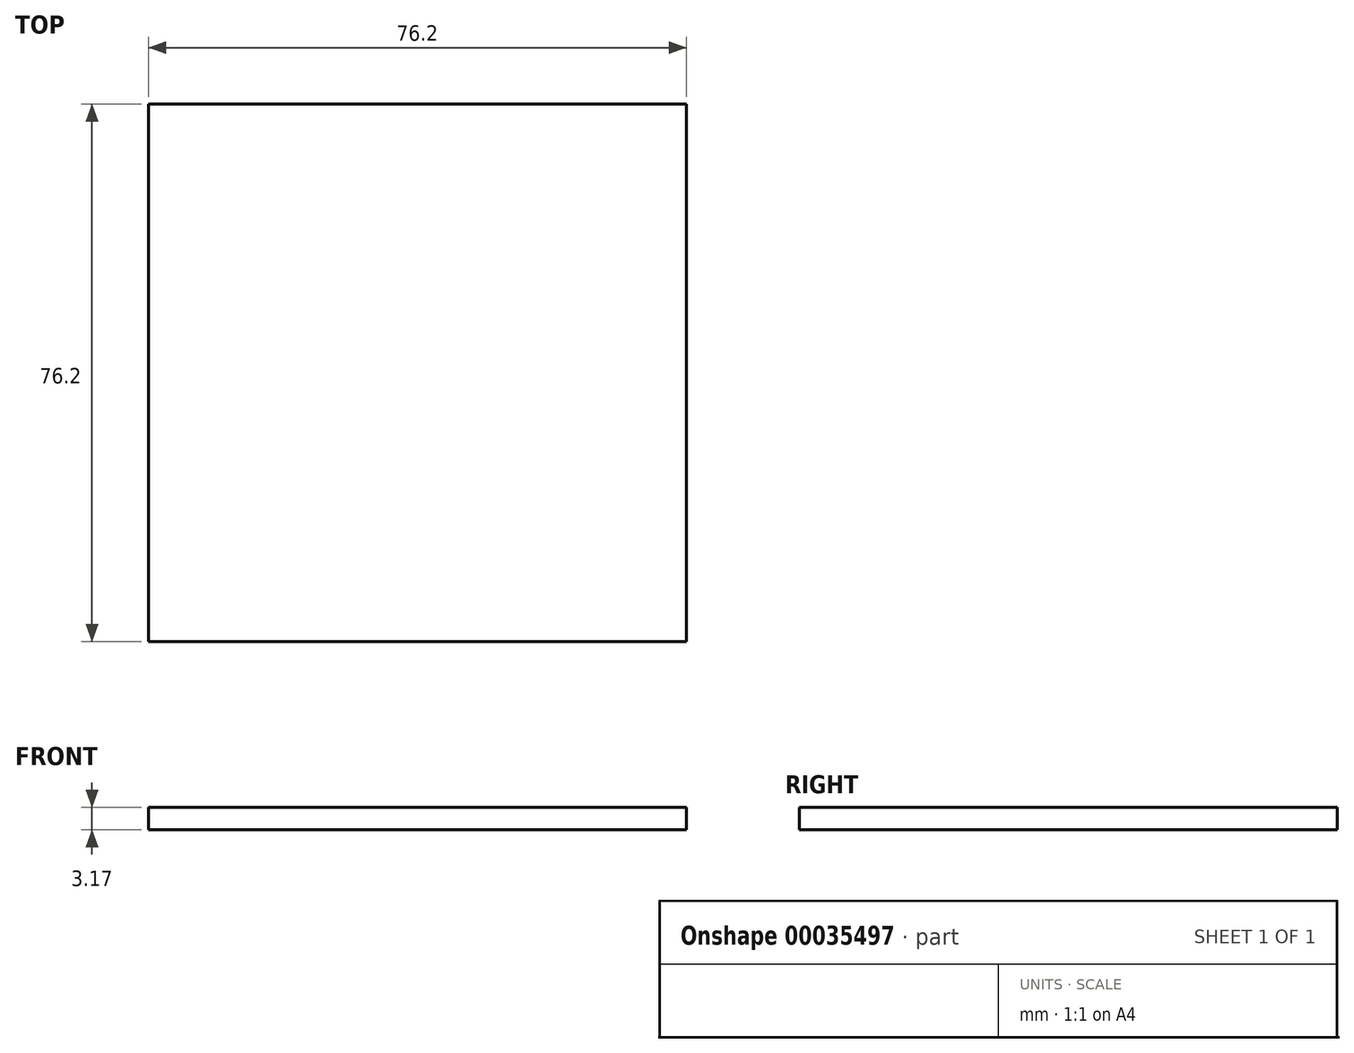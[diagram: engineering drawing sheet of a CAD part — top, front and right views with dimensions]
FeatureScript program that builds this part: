
annotation { "Feature Type Name" : "Feature", "Feature Type Description" : "" }
export const myFeature = defineFeature(function(context is Context, id is Id, definition is map)
    precondition{}
    {
        {
            var Q0;
            Q0=qCreatedBy(makeId("Top.planeOp"),FACE);
            var sketch = newSketch(context, id + "F0", { "sketchPlane" : qUnion([Q0])});
            skLineSegment(sketch, "E0.rect.bottom", {"start": v(38.1, -38.1) * mm, "end": v(-38.1, -38.1) * mm});
            skLineSegment(sketch, "E0.rect.top", {"start": v(38.1, 38.1) * mm, "end": v(-38.1, 38.1) * mm});
            skLineSegment(sketch, "E0.rect.left", {"start": v(38.1, -38.1) * mm, "end": v(38.1, 38.1) * mm});
            skLineSegment(sketch, "E0.rect.right", {"start": v(-38.1, -38.1) * mm, "end": v(-38.1, 38.1) * mm});
            skPoint(sketch, "E0.rect.middle", {"position": v(0, 0) * mm});
            skSolve(sketch);
        }
        {
            var Q0;
            Q0=makeQuery(id+"F0.imprint","IMPRINT",FACE,{"disambiguationData":[TD([[makeQuery(id+"F0.imprint","IMPRINT",EDGE,{"derivedFrom":sQuery(id+"F0.wireOp",EDGE,"E0.rect.bottom")}),-1.0]])]});
            extrude(context, id + "F1", {"entities" : qUnion([Q0]), "depth" : 3.17 * mm});
        }
    });
